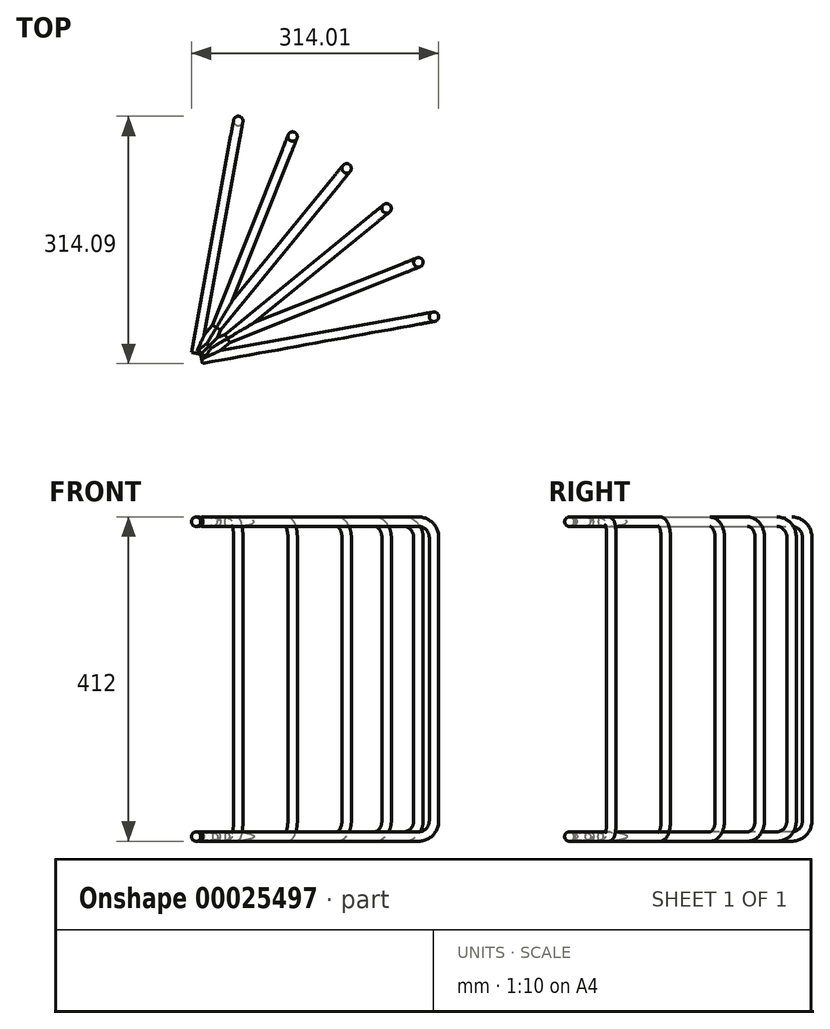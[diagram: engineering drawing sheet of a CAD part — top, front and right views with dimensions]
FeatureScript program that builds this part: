
annotation { "Feature Type Name" : "Feature", "Feature Type Description" : "" }
export const myFeature = defineFeature(function(context is Context, id is Id, definition is map)
    precondition{}
    {
        {
            var Q0;
            Q0=qCreatedBy(makeId("Top.planeOp"),FACE);
            var sketch = newSketch(context, id + "F0", { "sketchPlane" : qUnion([Q0])});
            skLineSegment(sketch, "E0", {"start": v(0.18, 0) * mm, "end": v(0.18, 2000) * mm});
            skLineSegment(sketch, "E1", {"start": v(0.18, 2000) * mm, "end": v(0.18, 0) * mm});
            skLineSegment(sketch, "E2", {"start": v(2000.18, 0) * mm, "end": v(0.18, 0) * mm});
            skLineSegment(sketch, "E3", {"start": v(0.18, 0) * mm, "end": v(275.81, 961.26) * mm, "construction": true});
            skLineSegment(sketch, "E4", {"start": v(0.18, 0) * mm, "end": v(707.28, 707.1) * mm, "construction": true});
            skLineSegment(sketch, "E5", {"start": v(961.44, 275.64) * mm, "end": v(0.18, 0) * mm, "construction": true});
            skCircle(sketch, "E6", {"center": v(0.18, 0) * mm, "radius": 300 * mm, "construction": true});
            skCircle(sketch, "E7", {"center": v(288.56, 82.7) * mm, "radius": 30 * mm, "construction": true});
            skCircle(sketch, "E8", {"center": v(212.3, 212.13) * mm, "radius": 30 * mm, "construction": true});
            skCircle(sketch, "E9", {"center": v(82.87, 288.38) * mm, "radius": 30 * mm, "construction": true});
            skLineSegment(sketch, "E10", {"start": v(0.18, 0) * mm, "end": v(295.37, 53.48) * mm, "construction": true});
            skLineSegment(sketch, "E11", {"start": v(278.85, 111.08) * mm, "end": v(0.18, 0) * mm, "construction": true});
            skLineSegment(sketch, "E12", {"start": v(0.18, 0) * mm, "end": v(232.43, 189.88) * mm, "construction": true});
            skLineSegment(sketch, "E13", {"start": v(190.06, 232.26) * mm, "end": v(0.18, 0) * mm, "construction": true});
            skLineSegment(sketch, "E14", {"start": v(111.26, 278.68) * mm, "end": v(0.18, 0) * mm, "construction": true});
            skLineSegment(sketch, "E15", {"start": v(53.65, 295.2) * mm, "end": v(0.18, 0) * mm, "construction": true});
            skLineSegment(sketch, "E16.0", {"start": v(1.08, -5.93) * mm, "end": v(296.27, 47.54) * mm, "construction": true});
            skLineSegment(sketch, "E17.0", {"start": v(276.48, 116.6) * mm, "end": v(-2.2, 5.51) * mm, "construction": true});
            skLineSegment(sketch, "E18.0", {"start": v(3.87, -4.73) * mm, "end": v(236.13, 185.15) * mm, "construction": true});
            skLineSegment(sketch, "E19.0", {"start": v(185.35, 235.97) * mm, "end": v(-4.54, 3.71) * mm, "construction": true});
            skLineSegment(sketch, "E20.0", {"start": v(47.74, 296.23) * mm, "end": v(-5.73, 1.04) * mm, "construction": true});
            skLineSegment(sketch, "E21.0", {"start": v(116.8, 276.4) * mm, "end": v(5.73, -2.28) * mm, "construction": true});
            skSolve(sketch);
        }
        {
            var Q0;
            Q0=sQuery(id+"F0.wireOp",EDGE,"E16.0");
            cPlane(context, id + "F1", {"entities" : qUnion([Q0]), "cplaneType" : CPlaneType.LINE_ANGLE, "offset" : 150 * mm, "angle" : 0 * degree, "width" : 150 * mm, "height" : 150 * mm});
        }
        {
            var Q0;
            Q0=qCreatedBy(id+"F1.planeOp",FACE);
            var sketch = newSketch(context, id + "F2", { "sketchPlane" : qUnion([Q0])});
            skLineSegment(sketch, "E22", {"start": v(0, 0) * mm, "end": v(-280, 0) * mm});
            skLineSegment(sketch, "E23", {"start": v(-300, 20) * mm, "end": v(-300, 380) * mm});
            skLineSegment(sketch, "E24", {"start": v(-280, 400) * mm, "end": v(0, 400) * mm});
            skPoint(sketch, "E25.visualSharp", {"position": v(-300, 400) * mm});
            skArc(sketch, "E25.filletArc", {"start": v(-280, 400) * mm, "mid": v(-294.14, 394.14) * mm, "end": v(-300, 380) * mm});
            skPoint(sketch, "E26.visualSharp", {"position": v(-300, 0) * mm});
            skArc(sketch, "E26.filletArc", {"start": v(-300, 20) * mm, "mid": v(-294.14, 5.86) * mm, "end": v(-280, 0) * mm});
            skSolve(sketch);
        }
        {
            var Q0;
            Q0=sQuery(id+"F2.wireOp",VERTEX,"E24.end");
            var Q1;
            Q1=sQuery(id+"F2.wireOp",EDGE,"E24");
            cPlane(context, id + "F3", {"entities" : qUnion([Q0, Q1]), "cplaneType" : CPlaneType.LINE_POINT, "offset" : 150 * mm, "width" : 150 * mm, "height" : 150 * mm});
        }
        {
            var Q0;
            Q0=qCreatedBy(id+"F3.planeOp",FACE);
            var sketch = newSketch(context, id + "F4", { "sketchPlane" : qUnion([Q0])});
            skPoint(sketch, "E27.0", {"position": v(6.03, 400) * mm});
            skCircle(sketch, "E28", {"center": v(6.03, 400) * mm, "radius": 6 * mm});
            skSolve(sketch);
        }
        {
            var Q0;
            Q0=makeQuery(id+"F4.imprint","IMPRINT",FACE,{"disambiguationData":[TD([[makeQuery(id+"F4.imprint","IMPRINT",EDGE,{"derivedFrom":sQuery(id+"F4.wireOp",EDGE,"E28")}),1.0]])]});
            var Q1;
            Q1=sQuery(id+"F2.wireOp",EDGE,"E24");
            var Q2;
            Q2=sQuery(id+"F2.wireOp",EDGE,"E25.filletArc");
            var Q3;
            Q3=sQuery(id+"F2.wireOp",EDGE,"E23");
            var Q4;
            Q4=sQuery(id+"F2.wireOp",EDGE,"E26.filletArc");
            var Q5;
            Q5=sQuery(id+"F2.wireOp",EDGE,"E22");
            sweep(context, id + "F5", {"profiles" : qUnion([Q0]), "path" : qUnion([Q1, Q2, Q3, Q4, Q5])});
        }
        {
            var Q0;
            Q0=sQuery(id+"F0.wireOp",EDGE,"E17.0");
            cPlane(context, id + "F6", {"entities" : qUnion([Q0]), "cplaneType" : CPlaneType.LINE_ANGLE, "offset" : 150 * mm, "angle" : 0 * degree, "width" : 150 * mm, "height" : 150 * mm});
        }
        {
            var Q0;
            Q0=qCreatedBy(id+"F6.planeOp",FACE);
            var sketch = newSketch(context, id + "F7", { "sketchPlane" : qUnion([Q0])});
            skLineSegment(sketch, "E29", {"start": v(0, 0) * mm, "end": v(280, 0) * mm});
            skLineSegment(sketch, "E30", {"start": v(300, 20) * mm, "end": v(300, 380) * mm});
            skLineSegment(sketch, "E31", {"start": v(280, 400) * mm, "end": v(0, 400) * mm});
            skPoint(sketch, "E32.visualSharp", {"position": v(300, 400) * mm});
            skArc(sketch, "E32.filletArc", {"start": v(300, 380) * mm, "mid": v(294.14, 394.14) * mm, "end": v(280, 400) * mm});
            skPoint(sketch, "E33.visualSharp", {"position": v(300, 0) * mm});
            skArc(sketch, "E33.filletArc", {"start": v(280, 0) * mm, "mid": v(294.14, 5.86) * mm, "end": v(300, 20) * mm});
            skSolve(sketch);
        }
        {
            var Q0;
            Q0=sQuery(id+"F7.wireOp",VERTEX,"E31.end");
            var Q1;
            Q1=sQuery(id+"F7.wireOp",EDGE,"E31");
            cPlane(context, id + "F8", {"entities" : qUnion([Q0, Q1]), "cplaneType" : CPlaneType.LINE_POINT, "offset" : 150 * mm, "width" : 150 * mm, "height" : 150 * mm});
        }
        {
            var Q0;
            Q0=qCreatedBy(id+"F8.planeOp",FACE);
            var sketch = newSketch(context, id + "F9", { "sketchPlane" : qUnion([Q0])});
            skPoint(sketch, "E34.0", {"position": v(-5.93, 400) * mm});
            skCircle(sketch, "E35", {"center": v(-5.93, 400) * mm, "radius": 6 * mm});
            skSolve(sketch);
        }
        {
            var Q0;
            Q0=makeQuery(id+"F9.imprint","IMPRINT",FACE,{"disambiguationData":[TD([[makeQuery(id+"F9.imprint","IMPRINT",EDGE,{"derivedFrom":sQuery(id+"F9.wireOp",EDGE,"E35")}),1.0]])]});
            var Q1;
            Q1=sQuery(id+"F7.wireOp",EDGE,"E31");
            var Q2;
            Q2=sQuery(id+"F7.wireOp",EDGE,"E32.filletArc");
            var Q3;
            Q3=sQuery(id+"F7.wireOp",EDGE,"E30");
            var Q4;
            Q4=sQuery(id+"F7.wireOp",EDGE,"E33.filletArc");
            var Q5;
            Q5=sQuery(id+"F7.wireOp",EDGE,"E29");
            sweep(context, id + "F10", {"operationType" : NewBodyOperationType.ADD, "profiles" : qUnion([Q0]), "path" : qUnion([Q1, Q2, Q3, Q4, Q5])});
        }
        {
            var Q0;
            Q0=qCreatedBy(makeId("Front.planeOp"),FACE);
            var sketch = newSketch(context, id + "F11", { "sketchPlane" : qUnion([Q0])});
            skLineSegment(sketch, "E36", {"start": v(0, 0) * mm, "end": v(0, 66.06) * mm, "construction": true});
            skSolve(sketch);
        }
        {
            var Q0;
            Q0=makeQuery(id+"F5.opSweep","SWEPT_BODY",BODY,{"disambiguationData":[OSD([sQuery(id+"F2.wireOp",EDGE,"E22"),sQuery(id+"F4.wireOp",EDGE,"E28")])]});
            var Q1;
            Q1=makeQuery(id+"F10.opSweep","SWEPT_BODY",BODY,{"disambiguationData":[OSD([sQuery(id+"F7.wireOp",EDGE,"E29"),sQuery(id+"F9.wireOp",EDGE,"E35")])]});
            var Q2;
            Q2=sQuery(id+"F11.wireOp",EDGE,"E36");
            circularPattern(context, id + "F12", {"operationType" : NewBodyOperationType.ADD, "entities" : qUnion([Q0, Q1]), "axis" : qUnion([Q2]), "angle" : 29 * degree, "instanceCount" : 3});
        }
    });
